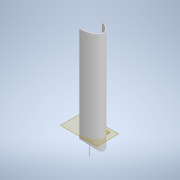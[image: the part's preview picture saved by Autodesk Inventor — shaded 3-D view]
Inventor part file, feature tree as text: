
AUTODESK INVENTOR PART (.ipt)
format: ipt  version: 2022 (Build 260153070, 153G)  size: 4,180,992 bytes
history: native  units: mm
features: sketch x9, extrude x9, plane x7, other x5, thicken_offset x3, fillet x2, projected_geometry x2, surface_op x1
ambient origin geometry x8: Origin, YZ Plane, XZ Plane, XY Plane, X Axis, Y Axis, Z Axis, Center Point
bodies: Body1 (feature_tree), Body2 (feature_tree), Body3 (feature_tree), Body4 (feature_tree)
feature tree (38):
  other  "Work Axis1"
  plane  "Work Plane1"
  sketch  "Sketch3"  dims[d10=1.5875mm d11=0.1mm d13=19.05mm]
  plane  "Work Plane3"
  thicken_offset  "Thicken2"
  thicken_offset  "Thicken6"
  other  "Work Axis3"
  plane  "Work Plane5"
  sketch  "Sketch6"  dims[d24=24.0mm d27=0.0mm d28=0.0mm d29=3.0mm d30=3.0mm]
  extrude  "Extrusion2"  Depth=10.0mm TaperAngle=0.0deg
  extrude  "Extrusion3"  TaperAngle=0.0deg  [1 undecoded]
  extrude  "Extrusion4"  Depth=19.05mm
  extrude  "Extrusion1"  Depth=395.5mm TaperAngle=0.0deg
  plane  "Work Plane9"
  fillet  "Fillet1"  Radius=5.0mm
  extrude  "Extrusion5"  Depth=40.0mm
  thicken_offset  "Thicken7"
  extrude  "Extrusion6"  TaperAngle=0.0deg  [1 undecoded]
  fillet  "Fillet2"  Radius=3.0mm
  extrude  "Extrusion7"  Depth=144.5mm TaperAngle=0.0deg
  plane  "Work Plane11"
  sketch  "Sketch1"  dims[d0=45.72mm d1=0.0mm d2=10.0mm d3=0.0mm]
  other  "Srf1"
  sketch  "Sketch2"  dims[d8=5.0mm d9=0.0mm]
  other  "Srf2"
  sketch  "Sketch4"  dims[d14=75.692mm d15=395.5mm d16=0.0mm d17=5.0mm]
  other  "Srf4"
  sketch  "Sketch5"  dims[d20=58.0mm d23=40.0mm]
  plane  "Work Plane8"
  sketch  "Sketch9"  dims[d31=200.0mm d32=144.5mm d33=0.0mm]
  projected_geometry  "Projected Loop1"
  sketch  "Sketch10"  dims[d34=250.0mm d35=0.0mm d36=3.0mm d37=2.0mm]
  projected_geometry  "Projected Loop2"
  sketch  "Sketch12"  dims[d38=2.0mm d39=0.0mm d40=3.0mm d41=5.0mm d42=2.0mm d43=0.0mm d44=2.0mm d45=40.0mm d46=15.0mm d47=5.0mm d48=2.0mm d49=0.0mm d50=1.75mm]
  plane  "Work Plane10"
  extrude  "ExtrusionSrf1"  Depth=3.0mm
  extrude  "ExtrusionSrf2"  Depth=3.0mm
  surface_op  "Boundary Patch2"
note: 2 required parameter values undecoded (feature->parameter linkage not recoverable at this tier; creation-order binding heuristic only, values carry confidence <= 0.55)
